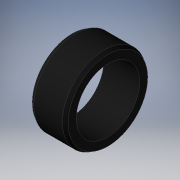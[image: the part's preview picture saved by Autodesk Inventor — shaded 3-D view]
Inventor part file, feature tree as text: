
AUTODESK INVENTOR PART (.ipt)
format: ipt  version: 2019 (Build 230136000, 136)  size: 131,072 bytes
history: native  units: mm
features: other x21, revolve x1, sketch x1
ambient origin geometry x8: Origin, YZ Plane, XZ Plane, XY Plane, X Axis, Y Axis, Z Axis, Center Point
bodies: Solid1 (feature_tree)
feature tree (23):
  revolve  "Revolution1"  [1 undecoded]
  other  "anbau_XY"
  other  "anbau_YZ"
  other  "anbau_ZX"
  other  "anbau_X"
  other  "anbau_Y"
  other  "anbau_Z"
  other  "anbau_Center"
  other  "insert_XY"
  other  "insert_YZ"
  other  "insert_ZX"
  other  "insert_X"
  other  "insert_Y"
  other  "insert_Z"
  other  "insert_Center"
  other  "schraube_punkt_XY"
  other  "schraube_punkt_YZ"
  other  "schraube_punkt_ZX"
  other  "schraube_punkt_X"
  other  "schraube_punkt_Y"
  other  "schraube_punkt_Z"
  other  "schraube_punkt_Center"
  sketch  "Sketch_1"  dims[d0=360.0deg d1=0.0mm d2=0.0mm d3=0.0mm]
note: 1 required parameter value undecoded (feature->parameter linkage not recoverable at this tier; creation-order binding heuristic only, values carry confidence <= 0.55)
